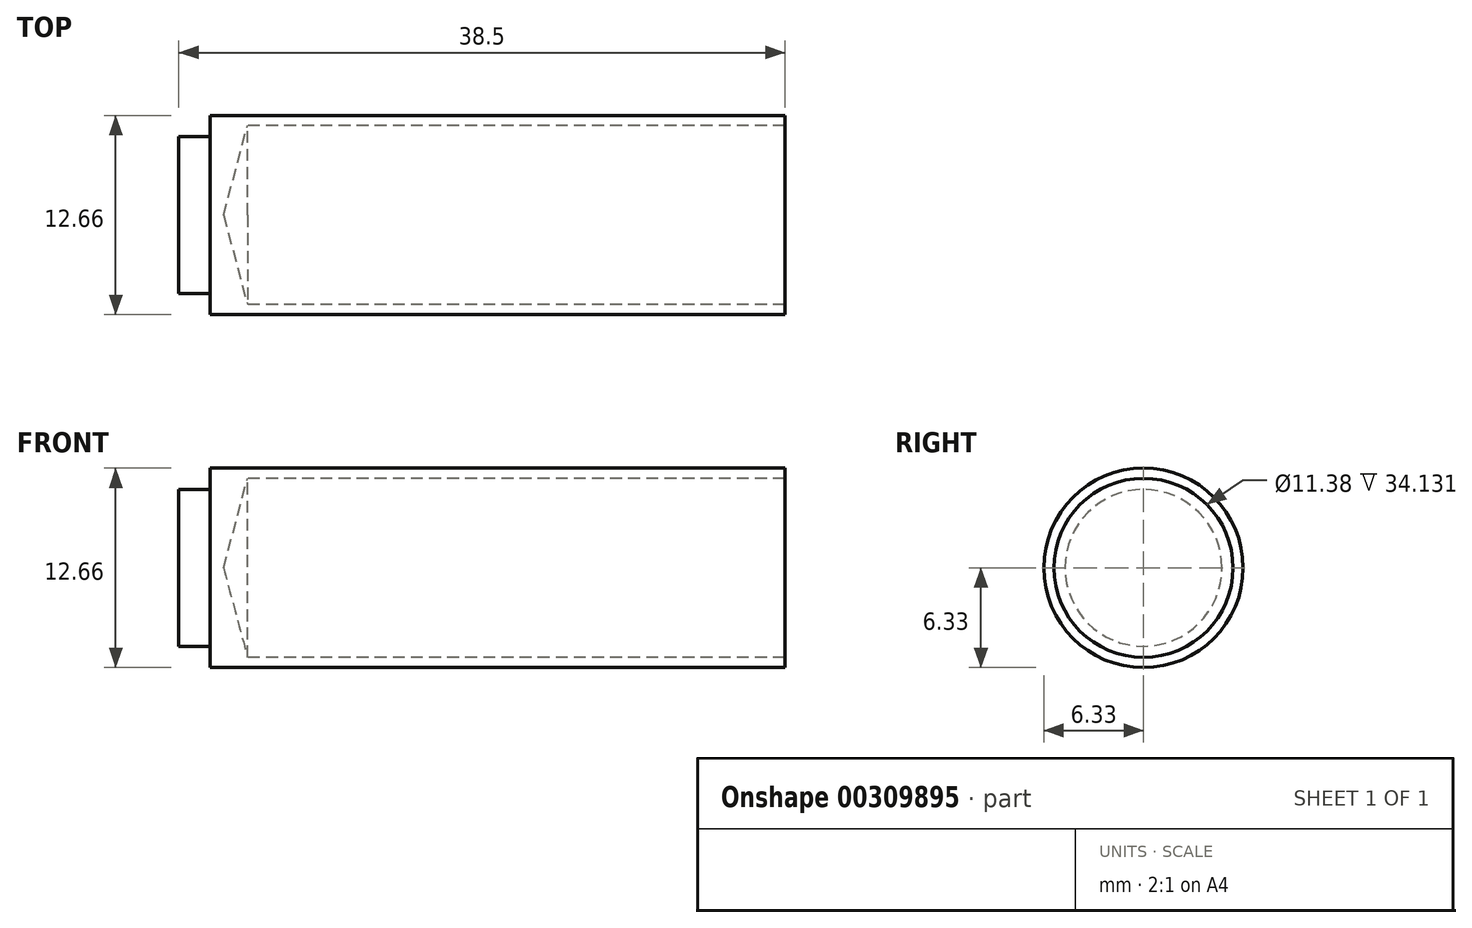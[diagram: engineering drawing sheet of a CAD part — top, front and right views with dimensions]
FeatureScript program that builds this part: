
annotation { "Feature Type Name" : "Feature", "Feature Type Description" : "" }
export const myFeature = defineFeature(function(context is Context, id is Id, definition is map)
    precondition{}
    {
        {
            var Q0;
            Q0=qCreatedBy(makeId("Front.planeOp"),FACE);
            var sketch = newSketch(context, id + "F0", { "sketchPlane" : qUnion([Q0])});
            skLineSegment(sketch, "E0", {"start": v(0, 0) * mm, "end": v(0, 4.98) * mm});
            skLineSegment(sketch, "E1", {"start": v(0, 4.98) * mm, "end": v(1.98, 4.98) * mm});
            skLineSegment(sketch, "E2", {"start": v(1.98, 4.98) * mm, "end": v(1.98, 6.33) * mm});
            skLineSegment(sketch, "E3", {"start": v(1.98, 6.33) * mm, "end": v(38.5, 6.33) * mm});
            skLineSegment(sketch, "E4", {"start": v(38.5, 6.33) * mm, "end": v(38.5, 5.69) * mm});
            skLineSegment(sketch, "E5", {"start": v(38.5, 5.69) * mm, "end": v(4.37, 5.69) * mm});
            skLineSegment(sketch, "E6", {"start": v(4.37, 5.69) * mm, "end": v(2.84, 0) * mm});
            skLineSegment(sketch, "E7", {"start": v(2.84, 0) * mm, "end": v(0, 0) * mm});
            skLineSegment(sketch, "E8", {"start": v(0, 0) * mm, "end": v(38.5, 0) * mm, "construction": true});
            skSolve(sketch);
        }
        {
            var Q0;
            Q0 = qSketchRegion(id + "F0", true);
            var Q1;
            Q1=sQuery(id+"F0.wireOp",EDGE,"E8");
            revolve(context, id + "F1", {"entities" : qUnion([Q0]), "axis" : qUnion([Q1]), "revolveType" : RevolveType.FULL});
        }
    });
